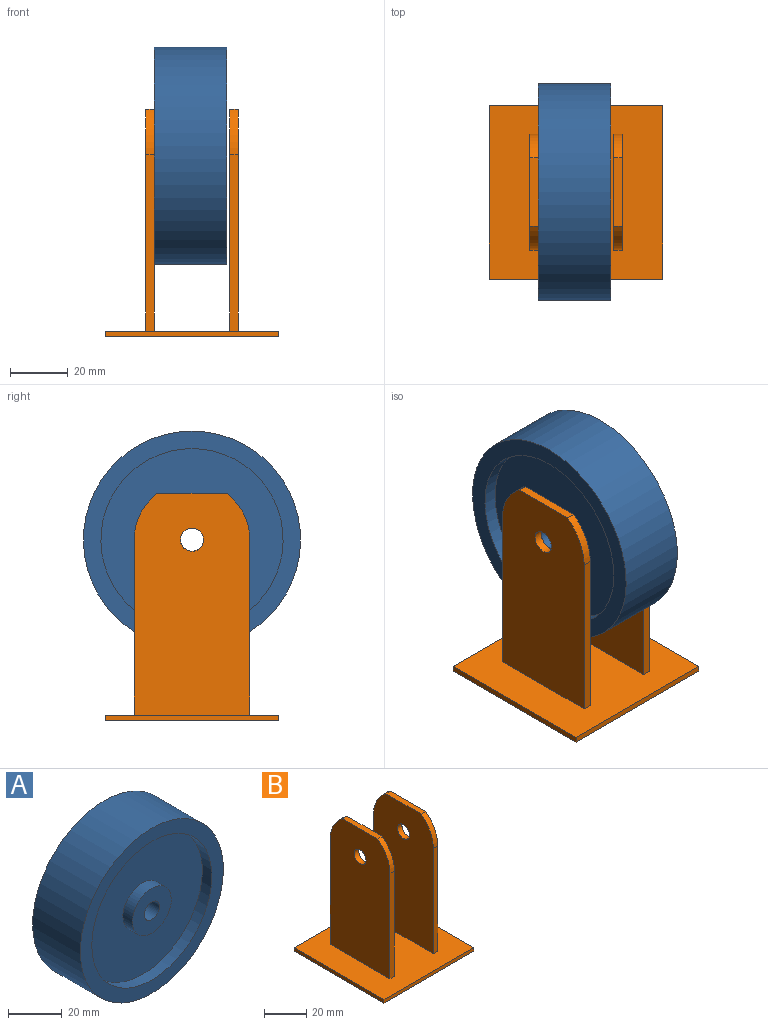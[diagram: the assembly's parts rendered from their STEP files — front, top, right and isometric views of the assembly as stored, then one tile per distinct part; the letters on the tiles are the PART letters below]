
ASSEMBLY  parts=2 mates=1
PART A: 12 faces, bbox 75x25x75 mm
  f0: cylinder r=37.5mm len=75mm, axis (0,1,0), area 5890.5mm2, adj f1,f10
  f1: plane 75x75mm, normal (0,-1,0), area 1304.6mm2, adj f0,f2
  f2: cylinder r=31.48mm len=62.96mm, axis (0,1,0), area 989mm2, adj f1,f3
  f3: plane 62.96x62.96mm, normal (0,-1,0), area 2787.4mm2, adj f2,f4
  f4: cylinder r=10.18mm len=20.37mm, axis (0,1,0), area 320mm2, adj f3,f5
  f5: plane 20.37x20.37mm, normal (0,-1,0), area 275.6mm2, adj f4,f11
  f6: plane 20.37x20.37mm, normal (0,1,0), area 275.6mm2, adj f7,f11
  f7: cylinder r=10.18mm len=20.37mm, axis (0,1,0), area 320mm2, adj f6,f8
  f8: plane 62.96x62.96mm, normal (0,1,0), area 2787.4mm2, adj f7,f9
  f9: cylinder r=31.48mm len=62.96mm, axis (0,1,0), area 989mm2, adj f8,f10
  f10: plane 75x75mm, normal (0,1,0), area 1304.6mm2, adj f0,f9
  f11: cylinder r=4mm len=25mm, axis (0,-1,0), area 628.3mm2, adj f5,f6
PART B: 22 faces, bbox 60x60x78.7 mm
  f0: plane 60.92x3mm, normal (0,-1,0), area 182.8mm2, adj f1,f3,f10,f20
  f1: plane 76.7x40mm, normal (1,0,0), area 2938.5mm2, adj f0,f2,f4,f10,f17,f20,f21
  f2: plane 60.92x3mm, normal (0,1,0), area 182.8mm2, adj f1,f3,f10,f21
  f3: plane 76.7x40mm, normal (-1,0,0), area 2938.5mm2, adj f0,f2,f4,f10,f17,f20,f21
  f4: plane 23.63x3mm, normal (0,0,1), area 70.9mm2, adj f1,f3,f20,f21
  f5: plane 60.92x3mm, normal (0,1,0), area 182.8mm2, adj f6,f8,f10,f19
  f6: plane 76.7x40mm, normal (-1,0,0), area 2938.5mm2, adj f5,f7,f9,f10,f16,f18,f19
  f7: plane 60.92x3mm, normal (0,-1,0), area 182.8mm2, adj f6,f8,f10,f18
  f8: plane 76.7x40mm, normal (1,0,0), area 2938.5mm2, adj f5,f7,f9,f10,f16,f18,f19
  f9: plane 23.63x3mm, normal (0,0,1), area 70.9mm2, adj f6,f8,f18,f19
  f10: plane 60x60mm, normal (0,0,1), area 3360mm2, adj f0,f1,f2,f3,f5,f6,f7,f8
  f11: plane 60x2mm, normal (0,-1,0), area 120mm2, adj f10,f12,f14,f15
  f12: plane 60x2mm, normal (1,0,0), area 120mm2, adj f10,f11,f13,f15
  f13: plane 60x2mm, normal (0,1,0), area 120mm2, adj f10,f12,f14,f15
  f14: plane 60x2mm, normal (-1,0,0), area 120mm2, adj f10,f11,f13,f15
  f15: plane 60x60mm, normal (0,0,-1), area 3600mm2, adj f11,f12,f13,f14
  f16: cylinder r=4mm len=8mm, axis (-1,0,0), area 75.4mm2, adj f6,f8
  f17: cylinder r=4mm len=8mm, axis (-1,0,0), area 75.4mm2, adj f1,f3
  f18: cylinder r=20mm len=15.78mm, axis (-1,0,0), area 55.3mm2, adj f6,f7,f8,f9
  f19: cylinder r=20mm len=15.78mm, axis (-1,0,0), area 55.3mm2, adj f5,f6,f8,f9
  f20: cylinder r=20mm len=15.78mm, axis (-1,0,0), area 55.3mm2, adj f0,f1,f3,f4
  f21: cylinder r=20mm len=15.78mm, axis (-1,0,0), area 55.3mm2, adj f1,f2,f3,f4
PLACE A rot(axis=(0,0,-1),90deg) t=(6.95,-26.86,77.78)mm
PLACE B t=(7.45,-26.86,15.22)mm fixed
MATE fastened A.f11 <-> B.f16  axis (-1,0,0) through (-5.55,-26.86,77.78)mm
